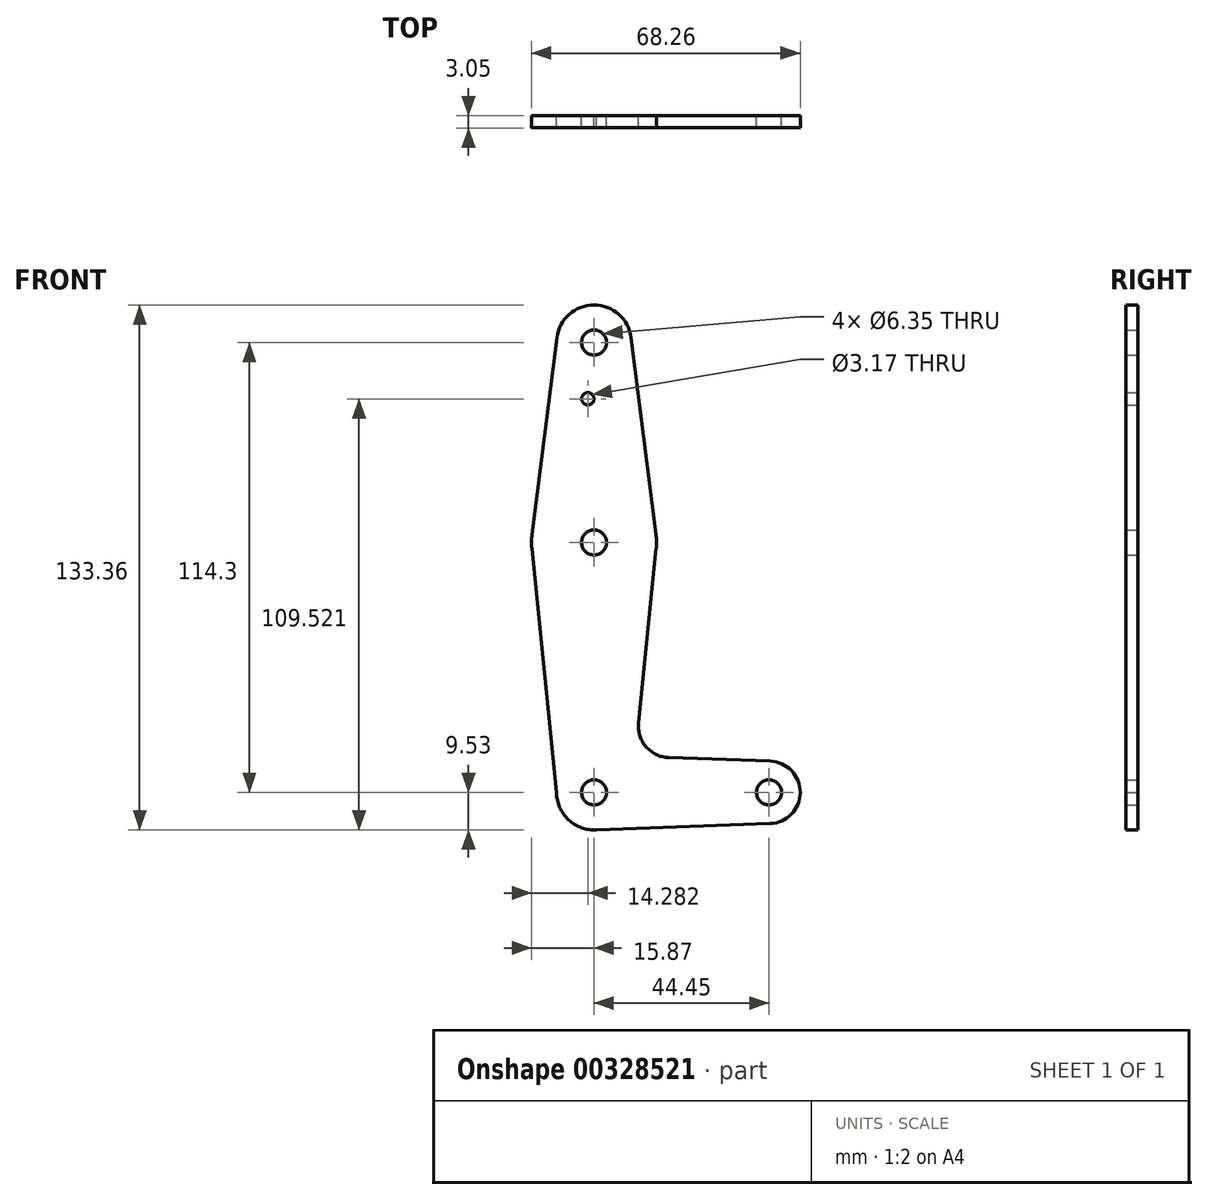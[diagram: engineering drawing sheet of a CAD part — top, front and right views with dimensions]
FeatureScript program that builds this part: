
annotation { "Feature Type Name" : "Feature", "Feature Type Description" : "" }
export const myFeature = defineFeature(function(context is Context, id is Id, definition is map)
    precondition{}
    {
        {
            var Q0;
            Q0=qCreatedBy(makeId("Front.planeOp"),FACE);
            var sketch = newSketch(context, id + "F0", { "sketchPlane" : qUnion([Q0])});
            skLineSegment(sketch, "E0", {"start": v(0, 0) * mm, "end": v(0, 114.3) * mm, "construction": true});
            skCircle(sketch, "E1", {"center": v(0, 0) * mm, "radius": 9.53 * mm});
            skCircle(sketch, "E2", {"center": v(0, 114.3) * mm, "radius": 9.53 * mm});
            skCircle(sketch, "E3", {"center": v(44.45, 0) * mm, "radius": 7.94 * mm});
            skCircle(sketch, "E4", {"center": v(0, 63.5) * mm, "radius": 15.88 * mm});
            skLineSegment(sketch, "E5", {"start": v(9.45, 115.5) * mm, "end": v(15.75, 65.48) * mm});
            skLineSegment(sketch, "E6", {"start": v(15.8, 61.9) * mm, "end": v(11.3, 17.6) * mm});
            skLineSegment(sketch, "E7", {"start": v(18.93, 8.85) * mm, "end": v(44.73, 7.93) * mm});
            skLineSegment(sketch, "E8", {"start": v(-9.53, 0) * mm, "end": v(-15.8, 61.9) * mm});
            skLineSegment(sketch, "E9", {"start": v(0, -9.53) * mm, "end": v(44.73, -7.93) * mm});
            skLineSegment(sketch, "E10", {"start": v(-9.45, 115.5) * mm, "end": v(-15.75, 65.48) * mm});
            skCircle(sketch, "E11", {"center": v(0, 0) * mm, "radius": 3.18 * mm});
            skCircle(sketch, "E12", {"center": v(44.45, 0) * mm, "radius": 3.18 * mm});
            skCircle(sketch, "E13", {"center": v(0, 63.5) * mm, "radius": 3.18 * mm});
            skCircle(sketch, "E14", {"center": v(0, 114.3) * mm, "radius": 3.18 * mm});
            skCircle(sketch, "E15", {"center": v(-1.59, 100) * mm, "radius": 1.59 * mm});
            skArc(sketch, "E16.filletArc", {"start": v(11.3, 17.6) * mm, "mid": v(13.22, 11.57) * mm, "end": v(18.93, 8.85) * mm});
            skLineSegment(sketch, "E17", {"start": v(0, 0) * mm, "end": v(44.45, 0) * mm, "construction": true});
            skSolve(sketch);
        }
        {
            var Q0;
            Q0 = qSketchRegion(id + "F0", true);
            extrude(context, id + "F1", {"entities" : qUnion([Q0]), "depth" : 3.05 * mm});
        }
    });
